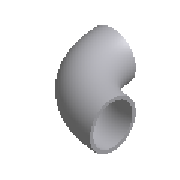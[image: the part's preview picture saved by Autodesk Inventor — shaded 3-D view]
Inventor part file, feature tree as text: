
AUTODESK INVENTOR PART (.ipt)
format: ipt  version: 2023.1 (Build 271208000, 208)  size: 174,592 bytes
history: native  units: mm (DEFAULTED — no unit token found)
features: other x4, sketch x2, sweep x1
ambient origin geometry x8: Origin, YZ Plane, XZ Plane, XY Plane, X Axis, Y Axis, Z Axis, Center Point
bodies: Solid1 (feature_tree)
feature tree (7):
  sweep  "Sweep1"
  other  "Work Point1"
  other  "Work Point2"
  other  "Work Axis1"
  other  "Work Axis2"
  sketch  "Sketch1"  dims[d0=56.3mm d1=60.3mm]
  sketch  "Sketch2"  dims[d2=76.0mm d3=76.0mm d4=0.0mm d5=0.0mm]
